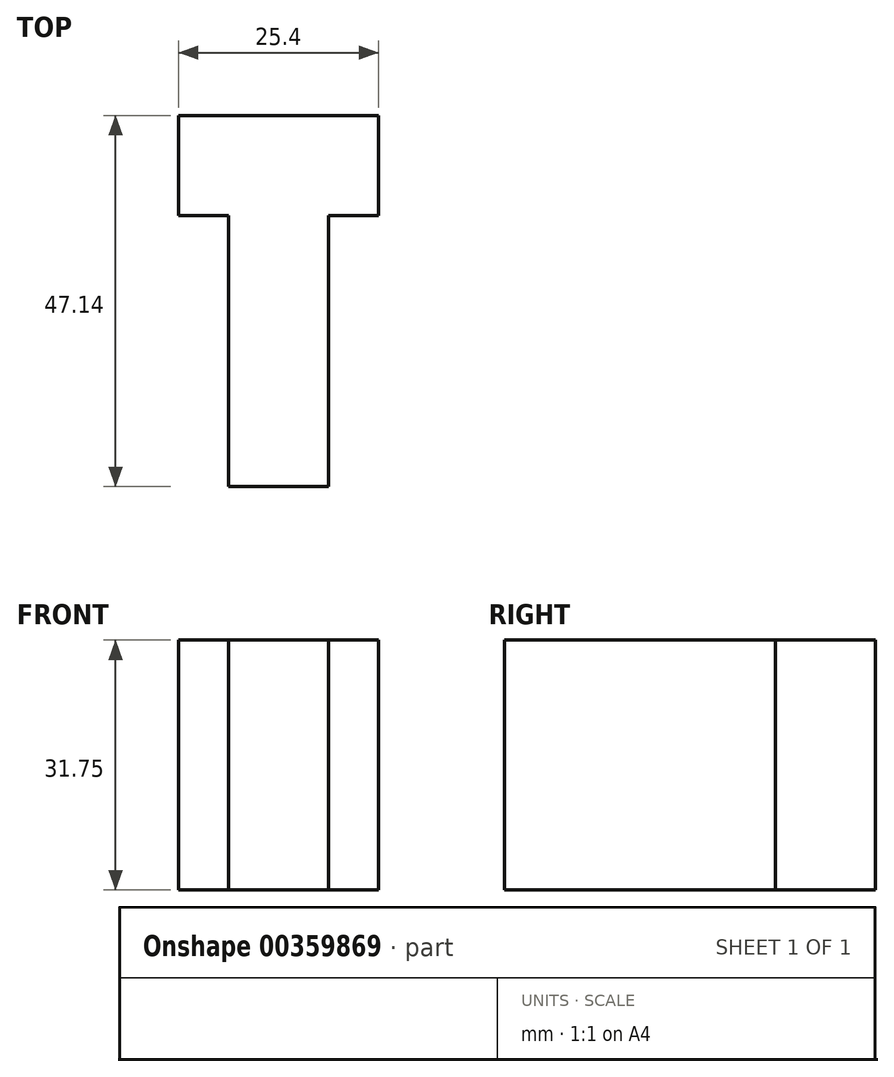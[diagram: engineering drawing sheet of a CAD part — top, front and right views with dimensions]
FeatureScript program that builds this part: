
annotation { "Feature Type Name" : "Feature", "Feature Type Description" : "" }
export const myFeature = defineFeature(function(context is Context, id is Id, definition is map)
    precondition{}
    {
        {
            var Q0;
            Q0=qCreatedBy(makeId("Top.planeOp"),FACE);
            var sketch = newSketch(context, id + "F0", { "sketchPlane" : qUnion([Q0])});
            skLineSegment(sketch, "E0", {"start": v(0, 0) * mm, "end": v(-6.35, 0) * mm});
            skLineSegment(sketch, "E1", {"start": v(-6.35, 0) * mm, "end": v(-6.35, 12.7) * mm});
            skLineSegment(sketch, "E2", {"start": v(19.05, 12.7) * mm, "end": v(19.05, 0) * mm});
            skLineSegment(sketch, "E3", {"start": v(19.05, 0) * mm, "end": v(12.7, 0) * mm});
            skLineSegment(sketch, "E4", {"start": v(12.7, 0) * mm, "end": v(12.7, -34.44) * mm});
            skLineSegment(sketch, "E5", {"start": v(12.7, -34.44) * mm, "end": v(0, -34.44) * mm});
            skLineSegment(sketch, "E6", {"start": v(0, 0) * mm, "end": v(0, -34.44) * mm});
            skLineSegment(sketch, "E7", {"start": v(-6.35, 12.7) * mm, "end": v(19.05, 12.7) * mm});
            skSolve(sketch);
        }
        {
            var Q0;
            Q0 = qSketchRegion(id + "F0", true);
            extrude(context, id + "F1", {"entities" : qUnion([Q0]), "depth" : 31.75 * mm});
        }
    });
